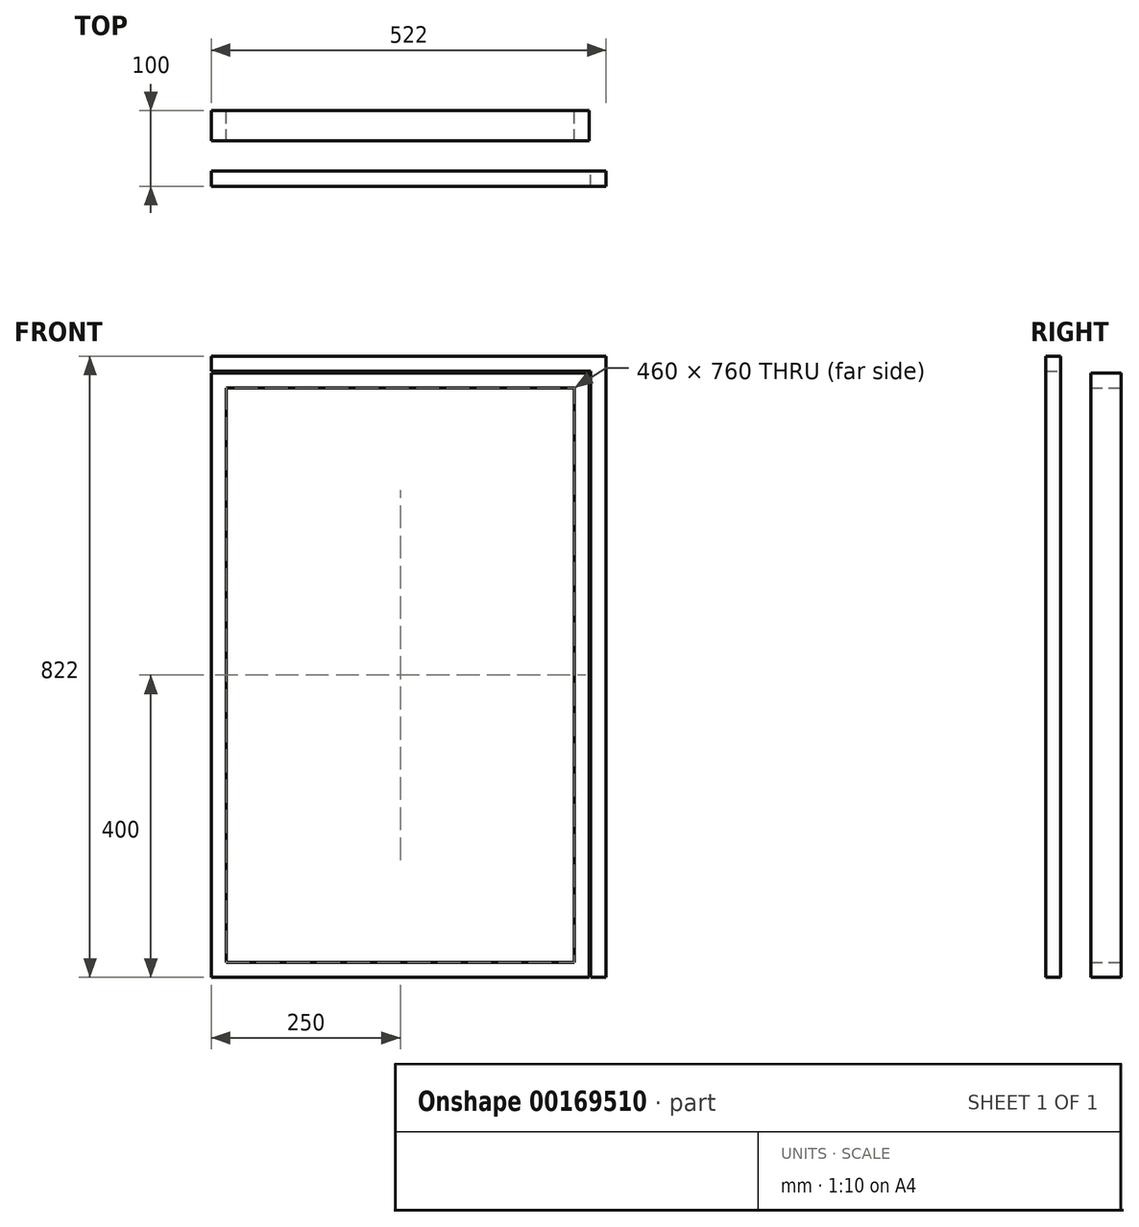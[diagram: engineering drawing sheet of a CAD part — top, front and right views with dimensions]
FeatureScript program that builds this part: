
annotation { "Feature Type Name" : "Feature", "Feature Type Description" : "" }
export const myFeature = defineFeature(function(context is Context, id is Id, definition is map)
    precondition{}
    {
        {
            var Q0;
            Q0=qCreatedBy(makeId("Front.planeOp"),FACE);
            var sketch = newSketch(context, id + "F0", { "sketchPlane" : qUnion([Q0])});
            skLineSegment(sketch, "E0.bottom", {"start": v(250, 400) * mm, "end": v(-250, 400) * mm});
            skLineSegment(sketch, "E0.top", {"start": v(250, -400) * mm, "end": v(-250, -400) * mm});
            skLineSegment(sketch, "E0.left", {"start": v(250, 400) * mm, "end": v(250, -400) * mm});
            skLineSegment(sketch, "E0.right", {"start": v(-250, 400) * mm, "end": v(-250, -400) * mm});
            skPoint(sketch, "E0.middle", {"position": v(0, 0) * mm});
            skLineSegment(sketch, "E1.bottom", {"start": v(230, 380) * mm, "end": v(-230, 380) * mm});
            skLineSegment(sketch, "E1.top", {"start": v(230, -380) * mm, "end": v(-230, -380) * mm});
            skLineSegment(sketch, "E1.left", {"start": v(230, 380) * mm, "end": v(230, -380) * mm});
            skLineSegment(sketch, "E1.right", {"start": v(-230, 380) * mm, "end": v(-230, -380) * mm});
            skSolve(sketch);
        }
        {
            var Q0;
            Q0 = qSketchRegion(id + "F0", true);
            extrude(context, id + "F1", {"entities" : qUnion([Q0]), "depth" : 40 * mm});
        }
        {
            var Q0;
            Q0=qCreatedBy(makeId("Front.planeOp"),FACE);
            cPlane(context, id + "F2", {"entities" : qUnion([Q0]), "cplaneType" : CPlaneType.OFFSET, "offset" : 80 * mm, "width" : 150 * mm, "height" : 150 * mm});
        }
        {
            var Q0;
            Q0=qCreatedBy(id+"F2.planeOp",FACE);
            var sketch = newSketch(context, id + "F3", { "sketchPlane" : qUnion([Q0])});
            skLineSegment(sketch, "E2.0", {"start": v(252, 402) * mm, "end": v(-250, 402) * mm});
            skLineSegment(sketch, "E2.1", {"start": v(252, 402) * mm, "end": v(252, -400) * mm});
            skLineSegment(sketch, "E3.0", {"start": v(272, 422) * mm, "end": v(272, -400) * mm});
            skLineSegment(sketch, "E3.1", {"start": v(272, 422) * mm, "end": v(-250, 422) * mm});
            skLineSegment(sketch, "E4", {"start": v(-250, 422) * mm, "end": v(-250, 402) * mm});
            skLineSegment(sketch, "E5", {"start": v(272, -400) * mm, "end": v(252, -400) * mm});
            skSolve(sketch);
        }
        {
            var Q0;
            Q0 = qSketchRegion(id + "F3", true);
            extrude(context, id + "F4", {"entities" : qUnion([Q0]), "depth" : 20 * mm});
        }
    });
